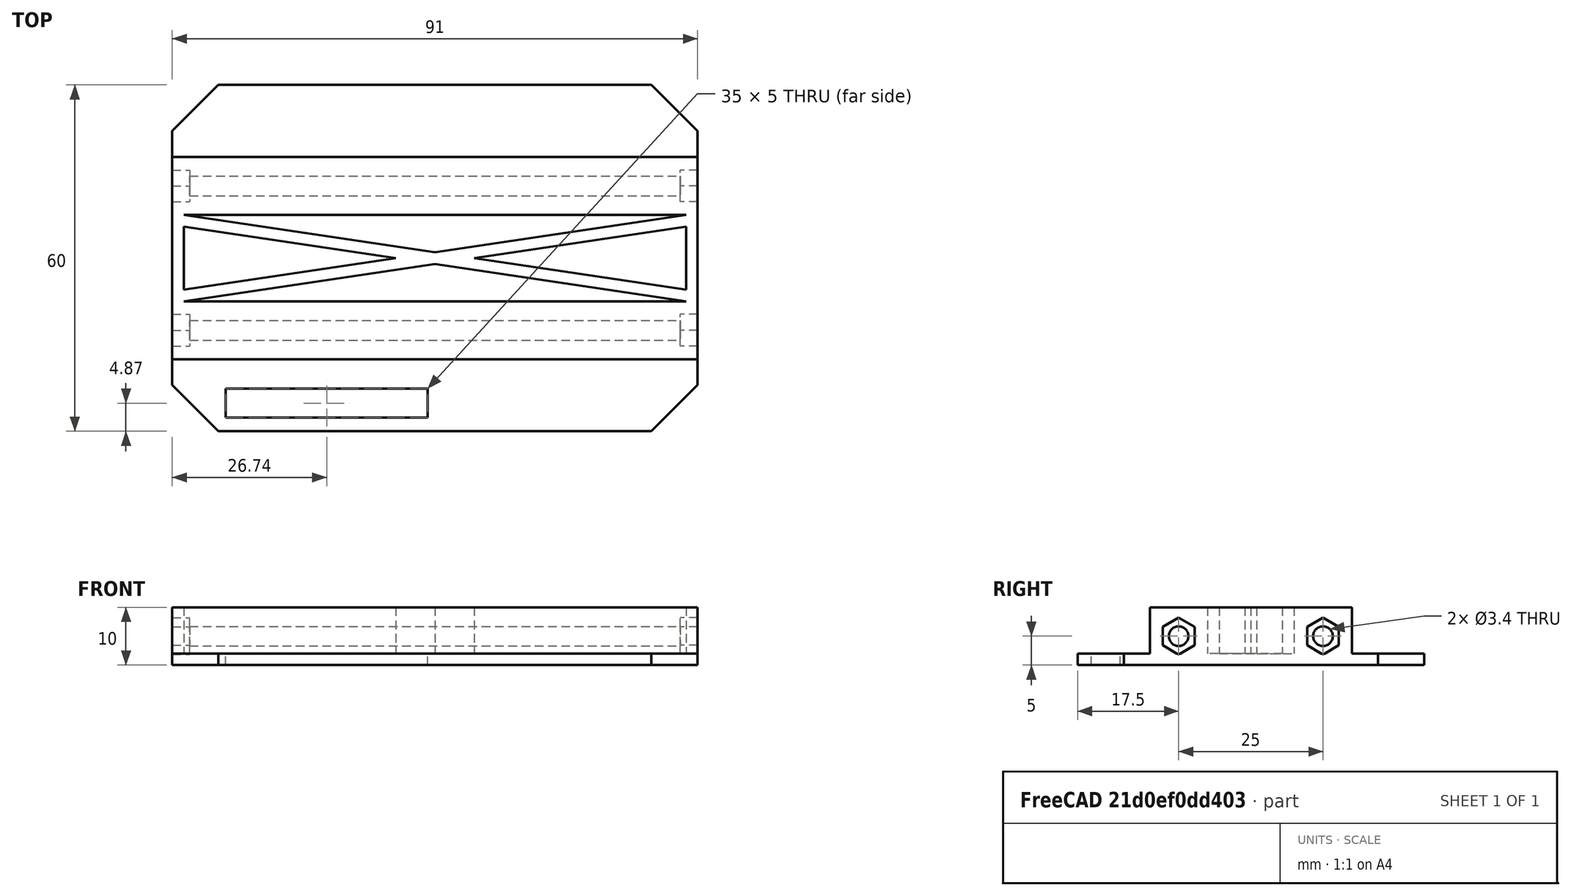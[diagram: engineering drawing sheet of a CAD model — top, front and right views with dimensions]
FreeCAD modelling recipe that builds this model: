
FCSTD DOCUMENT  (FreeCAD 0.21R33668 +26 (Git))
Label: Support_Display_new
License: All rights reserved
LicenseURL: https://en.wikipedia.org/wiki/All_rights_reserved
objects: Sketcher::SketchObject×7, PartDesign::Pocket×4, App::DocumentObjectGroup×3, PartDesign::CoordinateSystem×3, PartDesign::Pad×2, Spreadsheet::Sheet×1, PartDesign::Hole×1, App::FeaturePython×1, PartDesign::Chamfer×1, PartDesign::Body×1, App::Part×1, Mesh::Feature×1
note: 27 computed .brp shape members not serialized (recipe doc carries the construction recipe); baked Part::Feature solids carry a one-line shape summary decoded from their .brp
EXTERNAL_REF file=Display_Berrybase.FCStd obj=Spreadsheet

FEATURE [Spreadsheet::Sheet] Spreadsheet
  cells = B2='Carrier; E2='Display; B3='walls_thickness; C3(walls_thickness)==2 mm; E3='display_width; F3(display_width)==<<Display_Berrybase>>#<<Spreadsheet>>.width; H3='nut_width; I3(nut_width)==5.5 mm; B4='length; C4(length)==main_case_width - walls_thickness * 2; E4='display_height; F4(display_height)==<<Display_Berrybase>>#<<Spreadsheet>>.height; H4='nut_depth; I4(nut_depth)==3 mm; B5='height; C5(height)==10 mm; E5='display_depth; F5(display_depth)==<<Display_Berrybase>>#<<Spreadsheet>>.thickness; B6='width; C6(width)==60 mm; E6='connector_width; F6(connector_width)==<<Display_Berrybase>>#<<Spreadsheet>>.connector_width; H6='main_case_width; I6(main_case_width)==95 mm; B7='beams_width; C7(beams_width)==10 mm; E7='connector_height; F7(connector_height)==<<Display_Berrybase>>#<<Spreadsheet>>.connector_height; B8='beams_seperation; C8(beams_seperation)==15 mm; E8='connector_length; F8(connector_length)==<<Display_Berrybase>>#<<Spreadsheet>>.connector_length; B9='cross_thickness; C9(cross_thickness)==2 mm; E9='connector_offset_x; F9(connector_offset_x)==<<Display_Berrybase>>#<<Spreadsheet>>.connector_offset_x; B10='screw_radius; C10(screw_radius)==1.5 mm; E10='connector_offset_y; F10(connector_offset_y)==<<Display_Berrybase>>#<<Spreadsheet>>.connector_offset_y; B12='hole_clearance; C12(hole_clearance)==1 mm
FEATURE [Sketcher::SketchObject] Sketch
  FullyConstrained = true
  MapMode = 5
  Support = -> [XY_Plane]
  expr: Constraints[10] = Spreadsheet.width
  expr: Constraints[9] = Spreadsheet.length
  sketch-geometry (4):
    g0: LineSegment StartX=-45.5 StartY=30 StartZ=0 EndX=45.5 EndY=30 EndZ=0
    g1: LineSegment StartX=45.5 StartY=30 StartZ=0 EndX=45.5 EndY=-30 EndZ=0
    g2: LineSegment StartX=45.5 StartY=-30 StartZ=0 EndX=-45.5 EndY=-30 EndZ=0
    g3: LineSegment StartX=-45.5 StartY=-30 StartZ=0 EndX=-45.5 EndY=30 EndZ=0
  constraints (11):
    c: Coincident(g0,g1)
    c: Coincident(g1,g2)
    c: Coincident(g2,g3)
    c: Coincident(g3,g0)
    c: Horizontal(g0)
    c: Horizontal(g2)
    c: Vertical(g1)
    c: Vertical(g3)
    c: Symmetric(g0,g1,g-1)
    c: DistanceX(g0,g0) = 91
    c: DistanceY(g3,g3) = 60
FEATURE [PartDesign::Pad] Pad
  Direction = (0,0,1)
  Length = 2
  Length2 = 10
  Profile = -> Sketch
  ReferenceAxis = -> Sketch [N_Axis]
  Type = 0
  expr: Length = Spreadsheet.walls_thickness
FEATURE [Sketcher::SketchObject] Sketch001
  ExternalGeometry = -> [Pad]
  FullyConstrained = true
  MapMode = 5
  Placement = pos=(0,0,2) rot=(0,0,1;0rad)
  Support = -> [Pad]
  expr: Constraints[10] = Spreadsheet.beams_seperation + Spreadsheet.beams_width * 2
  sketch-geometry (4):
    g0: LineSegment StartX=-45.5 StartY=17.5 StartZ=0 EndX=45.5 EndY=17.5 EndZ=0
    g1: LineSegment StartX=45.5 StartY=17.5 StartZ=0 EndX=45.5 EndY=-17.5 EndZ=0
    g2: LineSegment StartX=45.5 StartY=-17.5 StartZ=0 EndX=-45.5 EndY=-17.5 EndZ=0
    g3: LineSegment StartX=-45.5 StartY=-17.5 StartZ=0 EndX=-45.5 EndY=17.5 EndZ=0
  constraints (11):
    c: Coincident(g0,g1)
    c: Coincident(g1,g2)
    c: Coincident(g2,g3)
    c: Coincident(g3,g0)
    c: Horizontal(g0)
    c: Horizontal(g2)
    c: Vertical(g1)
    c: PointOnObject(g0,g-4)
    c: PointOnObject(g1,g-6)
    c: Symmetric(g0,g2,g-1)
    c: DistanceY(g3,g3) = 35
FEATURE [PartDesign::Pad] Pad001
  BaseFeature = -> Pad
  Direction = (0,0,1)
  Length = 8
  Length2 = 10
  Profile = -> Sketch001
  ReferenceAxis = -> Sketch001 [N_Axis]
  Type = 0
  expr: Length = Spreadsheet.height - Spreadsheet.walls_thickness
FEATURE [Sketcher::SketchObject] Sketch002
  ExternalGeometry = -> [Pad001]
  FullyConstrained = true
  MapMode = 5
  Placement = pos=(0,0,10) rot=(0,0,1;0rad)
  Support = -> [Pad001]
  expr: Constraints[33] = Spreadsheet.beams_width
  expr: Constraints[34] = Spreadsheet.walls_thickness
  expr: Constraints[52] = Spreadsheet.cross_thickness
  sketch-geometry (21):
    g0: LineSegment StartX=-43.5 StartY=7.5 StartZ=0 EndX=43.5 EndY=7.5 EndZ=0
    g1: LineSegment StartX=43.5 StartY=7.5 StartZ=0 EndX=0 EndY=1.01106 EndZ=0
    g2: LineSegment StartX=0 StartY=1.01106 StartZ=0 EndX=-43.5 EndY=7.5 EndZ=0
    g3: LineSegment StartX=-43.5 StartY=5.47787 StartZ=0 EndX=-6.77789 EndY=0 EndZ=0
    g4: LineSegment StartX=-6.77789 StartY=0 StartZ=0 EndX=-43.5 EndY=-5.47787 EndZ=0
    g5: LineSegment StartX=-43.5 StartY=-5.47787 StartZ=0 EndX=-43.5 EndY=5.47787 EndZ=0
    g6: LineSegment StartX=-43.5 StartY=-7.5 StartZ=0 EndX=0 EndY=-1.01106 EndZ=0
    g7: LineSegment StartX=0 StartY=-1.01106 StartZ=0 EndX=43.5 EndY=-7.5 EndZ=0
    g8: LineSegment StartX=43.5 StartY=-7.5 StartZ=0 EndX=-43.5 EndY=-7.5 EndZ=0
    g9: LineSegment StartX=43.5 StartY=-5.47787 StartZ=0 EndX=6.77789 EndY=0 EndZ=0
    g10: LineSegment StartX=6.77789 StartY=0 StartZ=0 EndX=43.5 EndY=5.47787 EndZ=0
    g11: LineSegment StartX=43.5 StartY=5.47787 StartZ=0 EndX=43.5 EndY=-5.47787 EndZ=0
    g12: LineSegment StartX=-43.5 StartY=7.5 StartZ=0 EndX=43.5 EndY=7.5 EndZ=0
    g13: LineSegment StartX=43.5 StartY=7.5 StartZ=0 EndX=43.5 EndY=-7.5 EndZ=0
    g14: LineSegment StartX=43.5 StartY=-7.5 StartZ=0 EndX=-43.5 EndY=-7.5 EndZ=0
    g15: LineSegment StartX=-43.5 StartY=-7.5 StartZ=0 EndX=-43.5 EndY=7.5 EndZ=0
    g16: LineSegment StartX=0 StartY=1.01106 StartZ=0 EndX=6.77789 EndY=0 EndZ=0
    g17: LineSegment StartX=6.77789 StartY=0 StartZ=0 EndX=0 EndY=-1.01106 EndZ=0
    g18: LineSegment StartX=0 StartY=-1.01106 StartZ=0 EndX=-6.77789 EndY=0 EndZ=0
    g19: LineSegment StartX=-6.77789 StartY=0 StartZ=0 EndX=0 EndY=1.01106 EndZ=0
    g20: LineSegment StartX=-43.2049 StartY=7.45598 StartZ=0 EndX=-43.5 EndY=5.47787 EndZ=0
  constraints (54):
    c: Horizontal(g0)
    c: Coincident(g0,g1)
    c: PointOnObject(g1,g-2)
    c: Coincident(g1,g2)
    c: Coincident(g2,g0)
    c: PointOnObject(g3,g-1)
    c: Coincident(g3,g4)
    c: Coincident(g4,g5)
    c: Coincident(g5,g3)
    c: PointOnObject(g6,g-2)
    c: Coincident(g6,g7)
    c: Coincident(g7,g8)
    c: Coincident(g8,g6)
    c: Horizontal(g8)
    c: PointOnObject(g9,g-1)
    c: Coincident(g9,g10)
    c: Coincident(g10,g11)
    c: Coincident(g11,g9)
    c: Coincident(g12,g13)
    c: Coincident(g13,g14)
    c: Coincident(g14,g15)
    c: Coincident(g15,g12)
    c: Horizontal(g12)
    c: Horizontal(g14)
    c: Vertical(g15)
    c: PointOnObject(g3,g15)
    c: Coincident(g0,g12)
    c: Coincident(g6,g14)
    c: PointOnObject(g0,g13)
    c: PointOnObject(g10,g13)
    c: PointOnObject(g9,g13)
    c: PointOnObject(g7,g13)
    c: Symmetric(g0,g7,g-1)
    c: DistanceY(g0,g-4) = 10
    c: DistanceX(g-4,g0) = 2
    c: Symmetric(g3,g4,g-1)
    c: Symmetric(g10,g9,g-1)
    c: Coincident(g1,g16)
    c: Coincident(g16,g9)
    c: Coincident(g16,g17)
    c: Coincident(g17,g6)
    c: Coincident(g17,g18)
    c: Coincident(g18,g3)
    c: Coincident(g18,g19)
    c: Coincident(g19,g16)
    c: Parallel(g2,g16)
    c: Parallel(g16,g9)
    c: Parallel(g1,g19)
    c: Parallel(g19,g4)
    c: Parallel(g17,g10)
    c: PointOnObject(g20,g2)
    c: Perpendicular(g2,g20)
    c: Distance(g20) = 2
    c: Coincident(g20,g3)
FEATURE [PartDesign::Pocket] Pocket
  BaseFeature = -> Pad001
  Direction = (0,0,-1)
  Length = 8
  Length2 = 5
  Profile = -> Sketch002
  ReferenceAxis = -> Sketch002 [N_Axis]
  Type = 0
  expr: Length = Spreadsheet.height - Spreadsheet.walls_thickness
FEATURE [Sketcher::SketchObject] Sketch003
  ExternalGeometry = -> [Pocket]
  FullyConstrained = true
  MapMode = 5
  Placement = pos=(0,0,0) rot=(1,0,0;3.14159rad)
  Support = -> [Pocket]
  expr: Constraints[17] = <<Spreadsheet>>.display_width
  expr: Constraints[18] = <<Spreadsheet>>.display_height
  expr: Constraints[19] = (<<Spreadsheet>>.width - <<Spreadsheet>>.display_height) / 2 + <<Spreadsheet>>.connector_offset_y - <<Spreadsheet>>.hole_clearance
  expr: Constraints[20] = <<Spreadsheet>>.connector_height + <<Spreadsheet>>.hole_clearance
  expr: Constraints[21] = <<Spreadsheet>>.connector_width + <<Spreadsheet>>.hole_clearance
  expr: Constraints[22] = <<Spreadsheet>>.connector_offset_x - <<Spreadsheet>>.hole_clearance
  sketch-geometry (8):
    g0: LineSegment StartX=-42.26 StartY=27.63 StartZ=0 EndX=42.26 EndY=27.63 EndZ=0
    g1: LineSegment StartX=42.26 StartY=27.63 StartZ=0 EndX=42.26 EndY=-27.63 EndZ=0
    g2: LineSegment StartX=42.26 StartY=-27.63 StartZ=0 EndX=-42.26 EndY=-27.63 EndZ=0
    g3: LineSegment StartX=-42.26 StartY=-27.63 StartZ=0 EndX=-42.26 EndY=27.63 EndZ=0
    g4: LineSegment StartX=-36.26 StartY=27.63 StartZ=0 EndX=-1.26 EndY=27.63 EndZ=0
    g5: LineSegment StartX=-1.26 StartY=27.63 StartZ=0 EndX=-1.26 EndY=22.63 EndZ=0
    g6: LineSegment StartX=-1.26 StartY=22.63 StartZ=0 EndX=-36.26 EndY=22.63 EndZ=0
    g7: LineSegment StartX=-36.26 StartY=22.63 StartZ=0 EndX=-36.26 EndY=27.63 EndZ=0
  constraints (23):
    c: Coincident(g0,g1)
    c: Coincident(g1,g2)
    c: Coincident(g2,g3)
    c: Coincident(g3,g0)
    c: Horizontal(g0)
    c: Horizontal(g2)
    c: Vertical(g1)
    c: Vertical(g3)
    c: Coincident(g4,g5)
    c: Coincident(g5,g6)
    c: Coincident(g6,g7)
    c: Coincident(g7,g4)
    c: Horizontal(g4)
    c: Horizontal(g6)
    c: Vertical(g5)
    c: Vertical(g7)
    c: Symmetric(g0,g1,g-1)
    c: DistanceX(g0,g0) = 84.52
    c: DistanceY(g3,g3) = 55.26
    c: DistanceY(g4,g-4) = 2.37
    c: DistanceY(g7,g7) = 5
    c: DistanceX(g4,g4) = 35
    c: DistanceX(g0,g4) = 6
FEATURE [PartDesign::Pocket] Pocket001
  BaseFeature = -> Pocket
  Direction = (0,0,1)
  Length = 5
  Length2 = 5
  Profile = -> Sketch003
  ReferenceAxis = -> Sketch003 [N_Axis]
  Type = 1
FEATURE [Sketcher::SketchObject] Sketch004
  ExternalGeometry = -> [Pocket001]
  FullyConstrained = true
  MapMode = 5
  Placement = pos=(-45.5,0,0) rot=(0.57735,-0.57735,-0.57735;2.0944rad)
  Support = -> [Pocket001]
  expr: Constraints[10] = Spreadsheet.screw_radius
  expr: Constraints[11] = Spreadsheet.screw_radius
  expr: Constraints[6] = Spreadsheet.beams_width
  expr: Constraints[7] = Spreadsheet.beams_width
  sketch-geometry (4):
    g0: Circle CenterX=-12.5 CenterY=5 CenterZ=0 NormalX=0 NormalY=0 NormalZ=1 AngleXU=0 Radius=1.5
    g1: Circle CenterX=12.5 CenterY=5 CenterZ=0 NormalX=0 NormalY=0 NormalZ=1 AngleXU=0 Radius=1.5
    g2: LineSegment StartX=-7.5 StartY=10 StartZ=0 EndX=-7.5 EndY=0 EndZ=0
    g3: LineSegment StartX=7.5 StartY=10 StartZ=0 EndX=7.5 EndY=0 EndZ=0
  constraints (12):
    c: PointOnObject(g2,g-4)
    c: PointOnObject(g2,g-6)
    c: Vertical(g2)
    c: PointOnObject(g3,g-4)
    c: PointOnObject(g3,g-6)
    c: Vertical(g3)
    c: DistanceX(g-4,g2) = 10
    c: DistanceX(g3,g-5) = 10
    c: Symmetric(g-4,g2,g0)
    c: Symmetric(g-5,g3,g1)
    c: Radius(g0) = 1.5
    c: Radius(g1) = 1.5
FEATURE [PartDesign::Hole] Hole
  BaseFeature = -> Pocket001
  CustomThreadClearance = 0
  Depth = 221.105
  DepthType = 1
  Diameter = 3.4
  DrillForDepth = false
  DrillPoint = 1
  DrillPointAngle = 118
  HoleCutCountersinkAngle = 90
  HoleCutCustomValues = false
  HoleCutDepth = 0
  HoleCutDiameter = 6.1
  HoleCutType = 0
  ModelThread = false
  Profile = -> Sketch004
  Tapered = false
  TaperedAngle = 90
  ThreadClass = 0
  ThreadDepth = 221.105
  ThreadDepthType = 0
  ThreadDirection = 0
  ThreadFit = 0
  ThreadSize = 9
  ThreadType = 1
  Threaded = false
  UseCustomThreadClearance = false
FEATURE [Sketcher::SketchObject] Sketch005
  ExternalGeometry = -> [Hole]
  FullyConstrained = true
  MapMode = 5
  Placement = pos=(-45.5,0,0) rot=(0.57735,-0.57735,-0.57735;2.0944rad)
  Support = -> [Hole]
  expr: Constraints[36] = Spreadsheet.nut_width
  expr: Constraints[39] = Spreadsheet.nut_width
  sketch-geometry (14):
    g0: LineSegment StartX=-9.75 StartY=6.58771 StartZ=0 EndX=-12.5 EndY=8.17543 EndZ=0
    g1: LineSegment StartX=-12.5 StartY=8.17543 StartZ=0 EndX=-15.25 EndY=6.58771 EndZ=0
    g2: LineSegment StartX=-15.25 StartY=6.58771 StartZ=0 EndX=-15.25 EndY=3.41229 EndZ=0
    g3: LineSegment StartX=-15.25 StartY=3.41229 StartZ=0 EndX=-12.5 EndY=1.82457 EndZ=0
    g4: LineSegment StartX=-12.5 StartY=1.82457 StartZ=0 EndX=-9.75 EndY=3.41229 EndZ=0
    g5: LineSegment StartX=-9.75 StartY=3.41229 StartZ=0 EndX=-9.75 EndY=6.58771 EndZ=0
    g6: Circle CenterX=-12.5 CenterY=5 CenterZ=0 NormalX=0 NormalY=0 NormalZ=1 AngleXU=0 Radius=3.17543
    g7: LineSegment StartX=15.25 StartY=6.58771 StartZ=0 EndX=12.5 EndY=8.17543 EndZ=0
    g8: LineSegment StartX=12.5 StartY=8.17543 StartZ=0 EndX=9.75 EndY=6.58771 EndZ=0
    g9: LineSegment StartX=9.75 StartY=6.58771 StartZ=0 EndX=9.75 EndY=3.41229 EndZ=0
    g10: LineSegment StartX=9.75 StartY=3.41229 StartZ=0 EndX=12.5 EndY=1.82457 EndZ=0
    g11: LineSegment StartX=12.5 StartY=1.82457 StartZ=0 EndX=15.25 EndY=3.41229 EndZ=0
    g12: LineSegment StartX=15.25 StartY=3.41229 StartZ=0 EndX=15.25 EndY=6.58771 EndZ=0
    g13: Circle CenterX=12.5 CenterY=5 CenterZ=0 NormalX=0 NormalY=0 NormalZ=1 AngleXU=0 Radius=3.17543
  constraints (32):
    c: Coincident(g0,g1)
    c: Coincident(g1,g2)
    c: Coincident(g2,g3)
    c: Coincident(g3,g4)
    c: Coincident(g4,g5)
    c: Coincident(g5,g0)
    c: Equal(g0, g1-g5) x5
    c: PointOnObject(g0,g6)
    c: PointOnObject(g1,g6)
    c: PointOnObject(g2,g6)
    c: PointOnObject(g3,g6)
    c: PointOnObject(g4,g6)
    c: PointOnObject(g5,g6)
    c: Coincident(g6,g-3)
    c: Coincident(g7,g8)
    c: Coincident(g8,g9)
    c: Coincident(g9,g10)
    c: Coincident(g10,g11)
    c: Coincident(g11,g12)
    c: Coincident(g12,g7)
    c: Equal(g7, g8-g12) x5
    c: PointOnObject(g7,g13)
    c: PointOnObject(g8,g13)
    c: PointOnObject(g9,g13)
    c: PointOnObject(g10,g13)
    c: PointOnObject(g11,g13)
    c: PointOnObject(g12,g13)
    c: Coincident(g13,g-4)
    c: DistanceX(g1,g0) = 5.5
    c: Vertical(g5)
    c: Vertical(g9)
    c: DistanceX(g8,g7) = 5.5
FEATURE [PartDesign::Pocket] Pocket002
  BaseFeature = -> Hole
  Direction = (1,0,0)
  Length = 3
  Length2 = 5
  Profile = -> Sketch005
  ReferenceAxis = -> Sketch005 [N_Axis]
  Type = 0
  expr: Length = Spreadsheet.nut_depth
FEATURE [Sketcher::SketchObject] Sketch006
  ExternalGeometry = -> [Pocket002]
  FullyConstrained = true
  MapMode = 5
  Placement = pos=(45.5,0,0) rot=(0.57735,0.57735,0.57735;2.0944rad)
  Support = -> [Pocket002]
  expr: Constraints[38] = Spreadsheet.nut_width
  expr: Constraints[39] = Spreadsheet.nut_width
  sketch-geometry (14):
    g0: LineSegment StartX=-9.75 StartY=6.58771 StartZ=0 EndX=-12.5 EndY=8.17543 EndZ=0
    g1: LineSegment StartX=-12.5 StartY=8.17543 StartZ=0 EndX=-15.25 EndY=6.58771 EndZ=0
    g2: LineSegment StartX=-15.25 StartY=6.58771 StartZ=0 EndX=-15.25 EndY=3.41229 EndZ=0
    g3: LineSegment StartX=-15.25 StartY=3.41229 StartZ=0 EndX=-12.5 EndY=1.82457 EndZ=0
    g4: LineSegment StartX=-12.5 StartY=1.82457 StartZ=0 EndX=-9.75 EndY=3.41229 EndZ=0
    g5: LineSegment StartX=-9.75 StartY=3.41229 StartZ=0 EndX=-9.75 EndY=6.58771 EndZ=0
    g6: Circle CenterX=-12.5 CenterY=5 CenterZ=0 NormalX=0 NormalY=0 NormalZ=1 AngleXU=0 Radius=3.17543
    g7: LineSegment StartX=15.25 StartY=6.58771 StartZ=0 EndX=12.5 EndY=8.17543 EndZ=0
    g8: LineSegment StartX=12.5 StartY=8.17543 StartZ=0 EndX=9.75 EndY=6.58771 EndZ=0
    g9: LineSegment StartX=9.75 StartY=6.58771 StartZ=0 EndX=9.75 EndY=3.41229 EndZ=0
    g10: LineSegment StartX=9.75 StartY=3.41229 StartZ=0 EndX=12.5 EndY=1.82457 EndZ=0
    g11: LineSegment StartX=12.5 StartY=1.82457 StartZ=0 EndX=15.25 EndY=3.41229 EndZ=0
    g12: LineSegment StartX=15.25 StartY=3.41229 StartZ=0 EndX=15.25 EndY=6.58771 EndZ=0
    g13: Circle CenterX=12.5 CenterY=5 CenterZ=0 NormalX=0 NormalY=0 NormalZ=1 AngleXU=0 Radius=3.17543
  constraints (32):
    c: Coincident(g0,g1)
    c: Coincident(g1,g2)
    c: Coincident(g2,g3)
    c: Coincident(g3,g4)
    c: Coincident(g4,g5)
    c: Coincident(g5,g0)
    c: Equal(g0, g1-g5) x5
    c: PointOnObject(g0,g6)
    c: PointOnObject(g1,g6)
    c: PointOnObject(g2,g6)
    c: PointOnObject(g3,g6)
    c: PointOnObject(g4,g6)
    c: PointOnObject(g5,g6)
    c: Coincident(g6,g-3)
    c: Coincident(g7,g8)
    c: Coincident(g8,g9)
    c: Coincident(g9,g10)
    c: Coincident(g10,g11)
    c: Coincident(g11,g12)
    c: Coincident(g12,g7)
    c: Equal(g7, g8-g12) x5
    c: PointOnObject(g7,g13)
    c: PointOnObject(g8,g13)
    c: PointOnObject(g9,g13)
    c: PointOnObject(g10,g13)
    c: PointOnObject(g11,g13)
    c: PointOnObject(g12,g13)
    c: Coincident(g13,g-4)
    c: Vertical(g5)
    c: Vertical(g9)
    c: DistanceX(g1,g0) = 5.5
    c: DistanceX(g8,g7) = 5.5
FEATURE [PartDesign::Pocket] Pocket003
  BaseFeature = -> Pocket002
  Direction = (-1,0,0)
  Length = 3
  Length2 = 5
  Profile = -> Sketch006
  ReferenceAxis = -> Sketch006 [N_Axis]
  Type = 0
  expr: Length = Spreadsheet.nut_depth
FEATURE [App::DocumentObjectGroup] Parts
FEATURE [PartDesign::CoordinateSystem] LCS_Origin
  AttacherType = Attacher::AttachEngine3D
  MapMode = 2
  Support = -> [X_Axis001]
FEATURE [App::DocumentObjectGroup] Constraints
FEATURE [App::FeaturePython] Variables  # WARN: FeaturePython — macro-defined, semantics opaque (R4)
  Type = App::PropertyContainer
FEATURE [App::DocumentObjectGroup] Configurations
FEATURE [PartDesign::CoordinateSystem] LCS_side
  AttacherType = Attacher::AttachEngine3D
  MapMode = 11
  Placement = pos=(45.5,-12.5,5) rot=(0.57735,-0.57735,0.57735;4.18879rad)
  Support = -> [Pocket002]
FEATURE [PartDesign::CoordinateSystem] LCS_display
  AttacherType = Attacher::AttachEngine3D
  MapMode = 1
  Placement = pos=(-36.26,-27.63,0) rot=(0,0,1;0rad)
  Support = -> [Pocket002]
FEATURE [PartDesign::Chamfer] Chamfer
  Angle = 45
  Base = -> Pocket003 [Edge15,Edge1,Edge2,Edge17]
  BaseFeature = -> Pocket003
  ChamferType = 0
  FlipDirection = false
  Size = 8
  Size2 = 1
  SupportTransform = false
  UseAllEdges = false
FEATURE [PartDesign::Body] Body  label="Körper"
  Group = -> [Sketch,Pad,Sketch001,Pad001,Sketch002,Pocket,Sketch003,Pocket001,Sketch004,Hole,Sketch005,Pocket002,Sketch006,Pocket003,Chamfer]
  Origin = -> Origin
  Tip = -> Chamfer
FEATURE [App::Part] Model
  AssemblyType = Part::Link
  Group = -> [LCS_Origin,Constraints,Variables,Configurations,Body,LCS_side,LCS_display]
  Origin = -> Origin001
  Type = Assembly
FEATURE [Mesh::Feature] Mesh  label="Körper (Meshed)"
